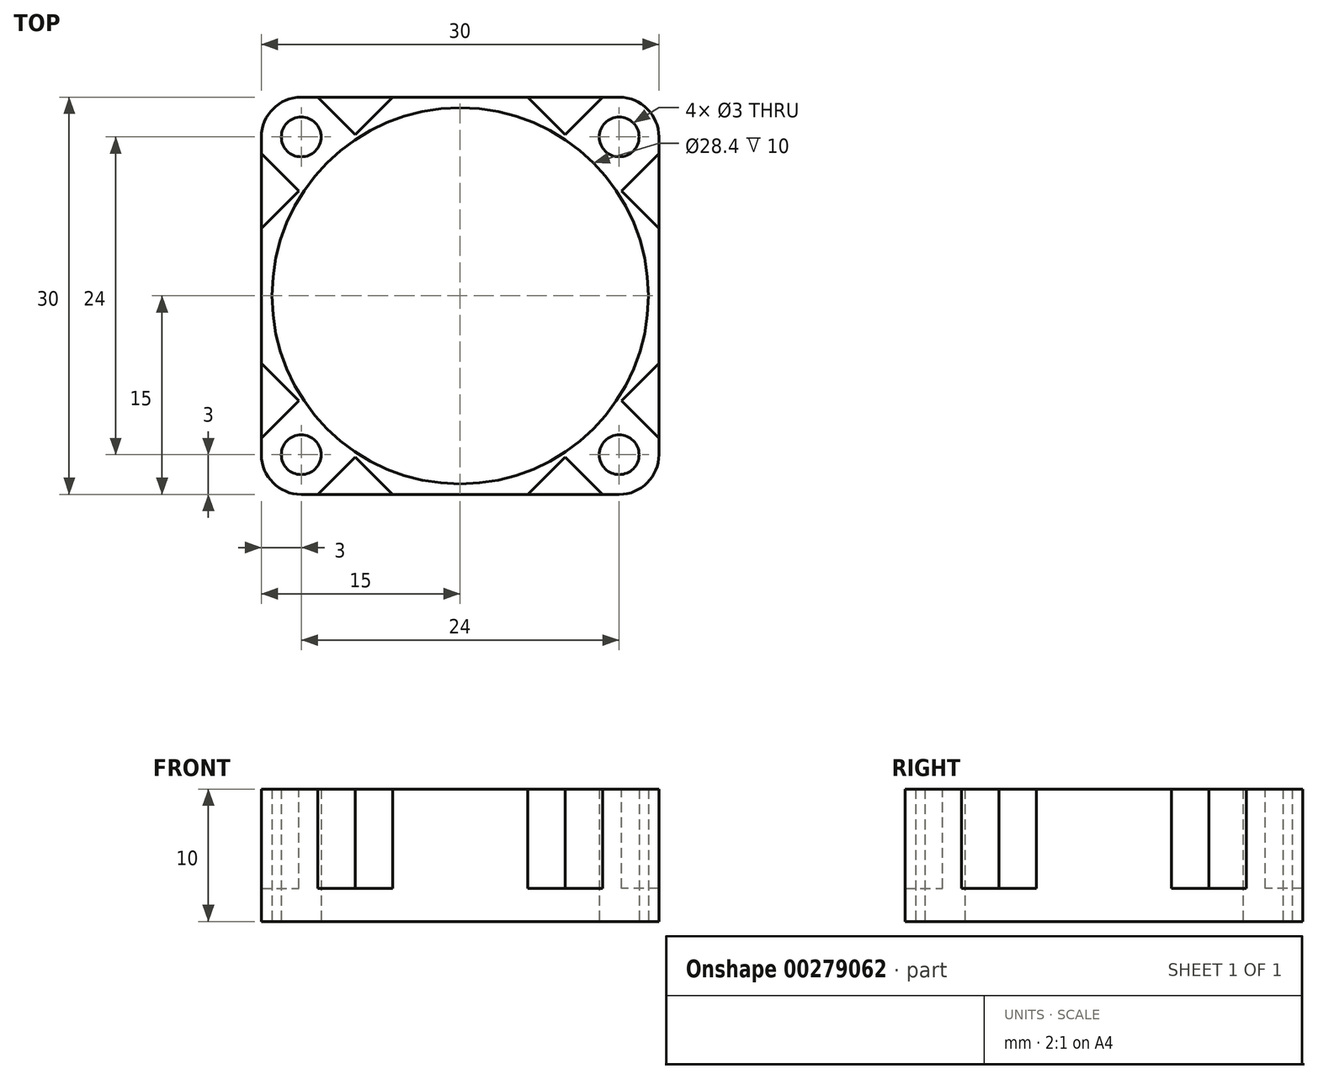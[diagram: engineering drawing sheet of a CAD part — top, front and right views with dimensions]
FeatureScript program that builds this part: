
annotation { "Feature Type Name" : "Feature", "Feature Type Description" : "" }
export const myFeature = defineFeature(function(context is Context, id is Id, definition is map)
    precondition{}
    {
        {
            var Q0;
            Q0=qCreatedBy(makeId("Top.planeOp"),FACE);
            var sketch = newSketch(context, id + "F0", { "sketchPlane" : qUnion([Q0])});
            skLineSegment(sketch, "E0.bottom", {"start": v(-12, 15) * mm, "end": v(12, 15) * mm});
            skLineSegment(sketch, "E0.top", {"start": v(-12, -15) * mm, "end": v(12, -15) * mm});
            skLineSegment(sketch, "E0.left", {"start": v(-15, 12) * mm, "end": v(-15, -12) * mm});
            skLineSegment(sketch, "E0.right", {"start": v(15, 12) * mm, "end": v(15, -12) * mm});
            skPoint(sketch, "E0.middle", {"position": v(0, 0) * mm});
            skLineSegment(sketch, "E1.bottom", {"start": v(-12, 12) * mm, "end": v(12, 12) * mm, "construction": true});
            skLineSegment(sketch, "E1.top", {"start": v(-12, -12) * mm, "end": v(12, -12) * mm, "construction": true});
            skLineSegment(sketch, "E1.left", {"start": v(-12, 12) * mm, "end": v(-12, -12) * mm, "construction": true});
            skLineSegment(sketch, "E1.right", {"start": v(12, 12) * mm, "end": v(12, -12) * mm, "construction": true});
            skCircle(sketch, "E2", {"center": v(-12, 12) * mm, "radius": 1.5 * mm});
            skCircle(sketch, "E3.1.0", {"center": v(-12, -12) * mm, "radius": 1.5 * mm});
            skCircle(sketch, "E3.2.0", {"center": v(12, -12) * mm, "radius": 1.5 * mm});
            skCircle(sketch, "E3.3.0", {"center": v(12, 12) * mm, "radius": 1.5 * mm});
            skPoint(sketch, "E4.visualSharp", {"position": v(-15, 15) * mm});
            skArc(sketch, "E4.filletArc", {"start": v(-12, 15) * mm, "mid": v(-14.12, 14.12) * mm, "end": v(-15, 12) * mm});
            skPoint(sketch, "E5.visualSharp", {"position": v(15, 15) * mm});
            skArc(sketch, "E5.filletArc", {"start": v(15, 12) * mm, "mid": v(14.12, 14.12) * mm, "end": v(12, 15) * mm});
            skPoint(sketch, "E6.visualSharp", {"position": v(15, -15) * mm});
            skArc(sketch, "E6.filletArc", {"start": v(12, -15) * mm, "mid": v(14.12, -14.12) * mm, "end": v(15, -12) * mm});
            skPoint(sketch, "E7.visualSharp", {"position": v(-15, -15) * mm});
            skArc(sketch, "E7.filletArc", {"start": v(-15, -12) * mm, "mid": v(-14.12, -14.12) * mm, "end": v(-12, -15) * mm});
            skCircle(sketch, "E8", {"center": v(0, 0) * mm, "radius": 14.2 * mm});
            skSolve(sketch);
        }
        {
            var Q0;
            Q0=qSketchRegion(id+"F0",true);
            extrude(context, id + "F1", {"entities" : qUnion([Q0]), "depth" : 10 * mm});
        }
        {
            var Q0;
            Q0=makeQuery(id+"F1.opExtrude","CAP_FACE",FACE,{"disambiguationData":[OSD([sQuery(id+"F0.wireOp",EDGE,"E0.bottom"),sQuery(id+"F0.wireOp",EDGE,"E0.top"),sQuery(id+"F0.wireOp",EDGE,"E0.left"),sQuery(id+"F0.wireOp",EDGE,"E0.right"),sQuery(id+"F0.wireOp",EDGE,"E2"),sQuery(id+"F0.wireOp",EDGE,"E3.1.0"),sQuery(id+"F0.wireOp",EDGE,"E3.2.0"),sQuery(id+"F0.wireOp",EDGE,"E3.3.0"),sQuery(id+"F0.wireOp",EDGE,"E4.filletArc"),sQuery(id+"F0.wireOp",EDGE,"E5.filletArc"),sQuery(id+"F0.wireOp",EDGE,"E6.filletArc"),sQuery(id+"F0.wireOp",EDGE,"E7.filletArc"),sQuery(id+"F0.wireOp",EDGE,"E8")])],"isStart":false});
            var sketch = newSketch(context, id + "F2", { "sketchPlane" : qUnion([Q0])});
            skLineSegment(sketch, "E9", {"start": v(-10.76, 15) * mm, "end": v(-7.93, 12.17) * mm});
            skLineSegment(sketch, "E10", {"start": v(-7.93, 12.17) * mm, "end": v(-5.1, 15) * mm});
            skLineSegment(sketch, "E11", {"start": v(0, 0) * mm, "end": v(-6, 6) * mm});
            skLineSegment(sketch, "E12", {"start": v(0, 0) * mm, "end": v(-6.66, 0) * mm});
            skLineSegment(sketch, "E13", {"start": v(-5.1, 15) * mm, "end": v(-10.76, 15) * mm});
            skLineSegment(sketch, "E14.MirrorCS", {"start": v(-12.17, 7.93) * mm, "end": v(-15, 5.1) * mm});
            skLineSegment(sketch, "E15.MirrorCS", {"start": v(-15, 5.1) * mm, "end": v(-15, 10.76) * mm});
            skLineSegment(sketch, "E16.MirrorCS", {"start": v(-15, 10.76) * mm, "end": v(-12.17, 7.93) * mm});
            skLineSegment(sketch, "E17", {"start": v(-13.06, 13.06) * mm, "end": v(-14.12, 14.12) * mm, "construction": true});
            skLineSegment(sketch, "E18", {"start": v(-10.94, 13.06) * mm, "end": v(-9.88, 14.12) * mm, "construction": true});
            skLineSegment(sketch, "E19.1.0", {"start": v(-15, -5.1) * mm, "end": v(-15, -10.76) * mm});
            skLineSegment(sketch, "E19.1.1", {"start": v(-10.76, -15) * mm, "end": v(-7.93, -12.17) * mm});
            skLineSegment(sketch, "E19.1.2", {"start": v(-5.1, -15) * mm, "end": v(-10.76, -15) * mm});
            skLineSegment(sketch, "E19.1.3", {"start": v(-7.93, -12.17) * mm, "end": v(-5.1, -15) * mm});
            skLineSegment(sketch, "E19.1.4", {"start": v(-12.17, -7.93) * mm, "end": v(-15, -5.1) * mm});
            skLineSegment(sketch, "E19.1.5", {"start": v(-15, -10.76) * mm, "end": v(-12.17, -7.93) * mm});
            skLineSegment(sketch, "E19.2.0", {"start": v(5.1, -15) * mm, "end": v(10.76, -15) * mm});
            skLineSegment(sketch, "E19.2.1", {"start": v(15, -10.76) * mm, "end": v(12.17, -7.93) * mm});
            skLineSegment(sketch, "E19.2.2", {"start": v(15, -5.1) * mm, "end": v(15, -10.76) * mm});
            skLineSegment(sketch, "E19.2.3", {"start": v(12.17, -7.93) * mm, "end": v(15, -5.1) * mm});
            skLineSegment(sketch, "E19.2.4", {"start": v(7.93, -12.17) * mm, "end": v(5.1, -15) * mm});
            skLineSegment(sketch, "E19.2.5", {"start": v(10.76, -15) * mm, "end": v(7.93, -12.17) * mm});
            skLineSegment(sketch, "E19.3.0", {"start": v(15, 5.1) * mm, "end": v(15, 10.76) * mm});
            skLineSegment(sketch, "E19.3.1", {"start": v(10.76, 15) * mm, "end": v(7.93, 12.17) * mm});
            skLineSegment(sketch, "E19.3.2", {"start": v(5.1, 15) * mm, "end": v(10.76, 15) * mm});
            skLineSegment(sketch, "E19.3.3", {"start": v(7.93, 12.17) * mm, "end": v(5.1, 15) * mm});
            skLineSegment(sketch, "E19.3.4", {"start": v(12.17, 7.93) * mm, "end": v(15, 5.1) * mm});
            skLineSegment(sketch, "E19.3.5", {"start": v(15, 10.76) * mm, "end": v(12.17, 7.93) * mm});
            skPoint(sketch, "E19.center", {"position": v(0, 0) * mm});
            skSolve(sketch);
        }
        {
            var Q0;
            Q0 = qSketchRegion(id + "F2", true);
            extrude(context, id + "F3", {"entities" : qUnion([Q0]), "operationType" : NewBodyOperationType.REMOVE, "oppositeDirection" : true, "depth" : 7.5 * mm});
        }
    });
